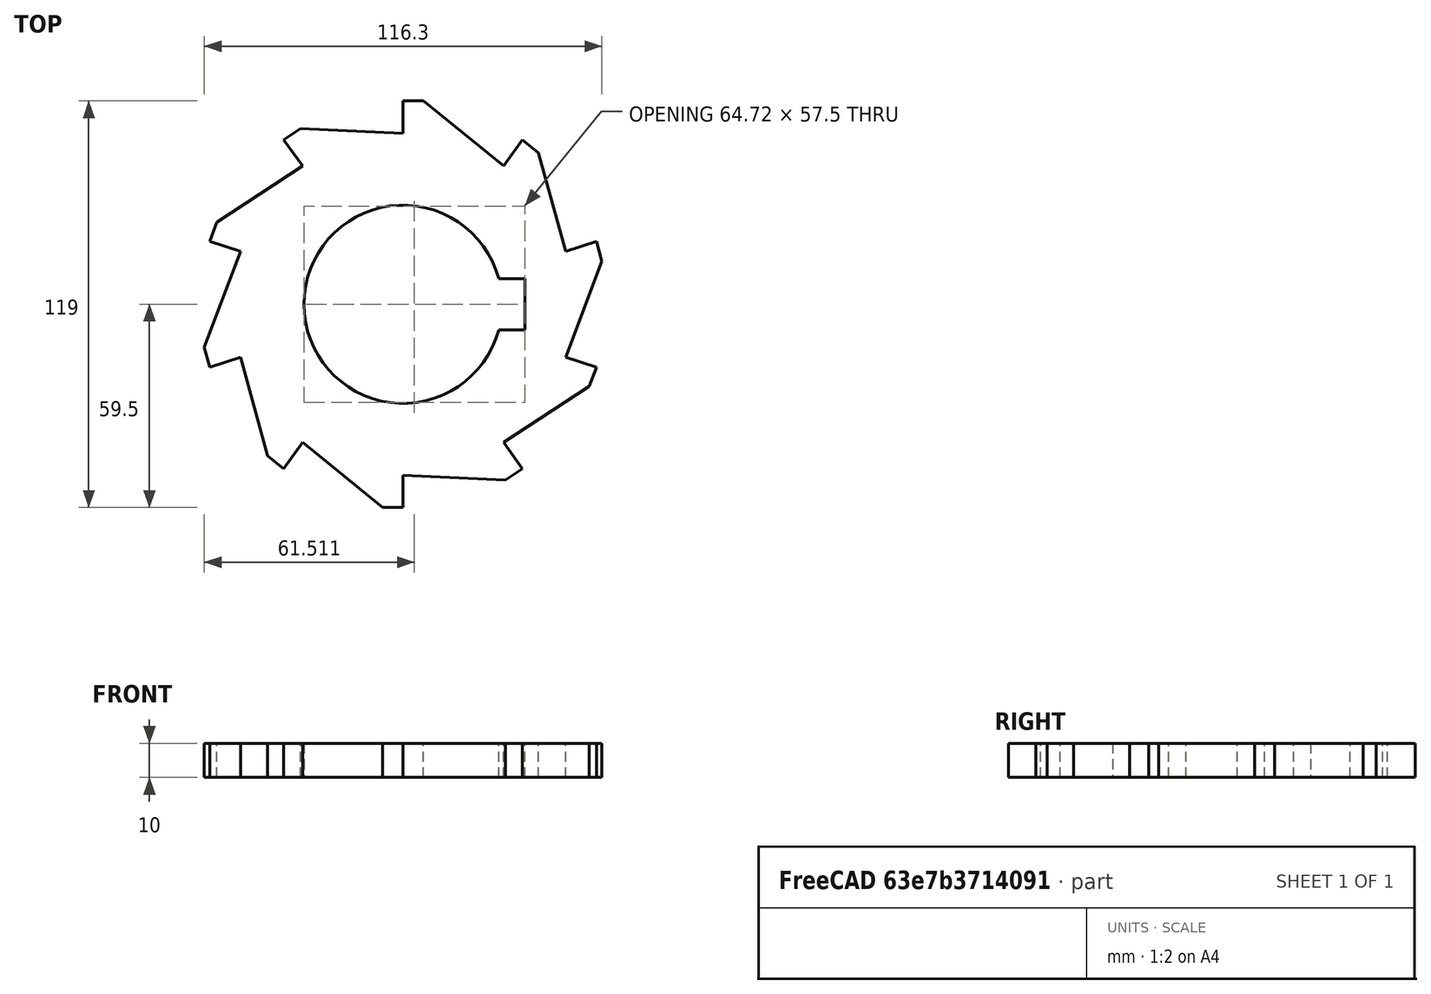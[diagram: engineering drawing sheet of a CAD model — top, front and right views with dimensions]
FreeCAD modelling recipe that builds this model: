
FCSTD DOCUMENT  (FreeCAD 0.20R29177 +426 (Git))
Label: 01 - Entrega de diseño de piezas
License: All rights reserved
LicenseURL: http://en.wikipedia.org/wiki/All_rights_reserved
objects: Sketcher::SketchObject×1, PartDesign::Pad×1, PartDesign::Body×1
note: 4 computed .brp shape members not serialized (recipe doc carries the construction recipe); baked Part::Feature solids carry a one-line shape summary decoded from their .brp

FEATURE [Sketcher::SketchObject] Sketch
  FullyConstrained = false
  MapMode = 5
  Support = -> [XY_Plane]
  sketch-geometry (47):
    g0: Circle CenterX=0 CenterY=0 CenterZ=0 NormalX=0 NormalY=0 NormalZ=1 AngleXU=0 Radius=59.5
    g1: ArcOfCircle CenterX=0 CenterY=0 CenterZ=0 NormalX=0 NormalY=0 NormalZ=1 AngleXU=0 Radius=29 StartAngle=0.261594 EndAngle=6.02159
    g2: LineSegment StartX=28.0134 StartY=7.5 StartZ=0 EndX=35.7211 EndY=7.5 EndZ=0
    g3: LineSegment StartX=35.7211 StartY=7.5 StartZ=0 EndX=35.7211 EndY=-7.5 EndZ=0
    g4: LineSegment StartX=35.7211 StartY=-7.5 StartZ=0 EndX=28.0134 EndY=-7.5 EndZ=0
    g5: Circle CenterX=0 CenterY=0 CenterZ=0 NormalX=0 NormalY=0 NormalZ=1 AngleXU=0 Radius=50
    g6: LineSegment StartX=-1.00329e-05 StartY=59.5 StartZ=0 EndX=5.99999 EndY=59.5 EndZ=0
    g7: LineSegment StartX=0 StartY=0 StartZ=0 EndX=81.4793 EndY=26.4742 EndZ=0
    g8: LineSegment StartX=0 StartY=0 StartZ=0 EndX=48.9757 EndY=67.4093 EndZ=0
    g9: LineSegment StartX=47.5528 StartY=15.4508 StartZ=0 EndX=56.5879 EndY=18.3865 EndZ=0
    g10: LineSegment StartX=0 StartY=0 StartZ=0 EndX=98.3194 EndY=0 EndZ=0
    g11: LineSegment StartX=0 StartY=0 StartZ=0 EndX=-40.9797 EndY=56.4037 EndZ=0
    g12: LineSegment StartX=0 StartY=0 StartZ=0 EndX=-69.3926 EndY=22.547 EndZ=0
    g13: LineSegment StartX=0 StartY=0 StartZ=0 EndX=-74.8837 EndY=-24.3312 EndZ=0
    g14: LineSegment StartX=0 StartY=0 StartZ=0 EndX=-41.6429 EndY=-57.3166 EndZ=0
    g15: LineSegment StartX=0 StartY=0 StartZ=0 EndX=-2.51e-14 EndY=-71.5915 EndZ=0
    g16: LineSegment StartX=0 StartY=0 StartZ=0 EndX=39.8031 EndY=-54.7843 EndZ=0
    g17: LineSegment StartX=0 StartY=0 StartZ=0 EndX=82.7007 EndY=-26.8711 EndZ=0
    g18: LineSegment StartX=56.5879 StartY=18.3865 StartZ=0 EndX=58.1519 EndY=12.5939 EndZ=0
    g19: LineSegment StartX=58.1519 StartY=12.5939 StartZ=0 EndX=47.5528 EndY=-15.4508 EndZ=0
    g20: LineSegment StartX=47.5528 StartY=-15.4508 StartZ=0 EndX=56.5879 EndY=-18.3865 EndZ=0
    g21: LineSegment StartX=56.5879 StartY=-18.3865 StartZ=0 EndX=54.4484 EndY=-23.9921 EndZ=0
    g22: LineSegment StartX=54.4484 StartY=-23.9921 StartZ=0 EndX=29.3893 EndY=-40.4508 EndZ=0
    g23: LineSegment StartX=29.3893 StartY=-40.4508 StartZ=0 EndX=34.9732 EndY=-48.1365 EndZ=0
    g24: LineSegment StartX=34.9732 StartY=-48.1365 StartZ=0 EndX=29.9475 EndY=-51.414 EndZ=0
    g25: LineSegment StartX=29.9475 StartY=-51.414 StartZ=0 EndX=-1.78e-14 EndY=-50 EndZ=0
    g26: LineSegment StartX=-1.78e-14 StartY=-50 StartZ=0 EndX=-2.09e-14 EndY=-59.5 EndZ=0
    g27: LineSegment StartX=-6 StartY=-59.5 StartZ=0 EndX=-29.3893 EndY=-40.4508 EndZ=0
    g28: LineSegment StartX=-47.5528 StartY=-15.4508 StartZ=0 EndX=-56.5879 EndY=-18.3865 EndZ=0
    g29: LineSegment StartX=-56.5879 StartY=-18.3865 StartZ=0 EndX=-58.1519 EndY=-12.5939 EndZ=0
    g30: LineSegment StartX=-58.1519 StartY=-12.5939 StartZ=0 EndX=-47.5528 EndY=15.4508 EndZ=0
    g31: LineSegment StartX=-47.5528 StartY=15.4508 StartZ=0 EndX=-56.5879 EndY=18.3865 EndZ=0
    g32: LineSegment StartX=-56.5879 StartY=18.3865 StartZ=0 EndX=-54.4484 EndY=23.9921 EndZ=0
    g33: LineSegment StartX=-54.4484 StartY=23.9921 StartZ=0 EndX=-29.3893 EndY=40.4508 EndZ=0
    g34: LineSegment StartX=-29.3893 StartY=40.4508 StartZ=0 EndX=-34.9732 EndY=48.1365 EndZ=0
    g35: LineSegment StartX=-2.09e-14 StartY=-59.5 StartZ=0 EndX=-6 EndY=-59.5 EndZ=0
    g36: LineSegment StartX=-34.9732 StartY=-48.1365 StartZ=0 EndX=-39.6433 EndY=-44.3695 EndZ=0
    g37: LineSegment StartX=-39.6433 StartY=-44.3695 StartZ=0 EndX=-47.5528 EndY=-15.4508 EndZ=0
    g38: LineSegment StartX=-34.9732 StartY=48.1365 StartZ=0 EndX=-29.9475 EndY=51.414 EndZ=0
    g39: LineSegment StartX=-29.9475 StartY=51.414 StartZ=0 EndX=-1.00329e-05 EndY=50 EndZ=0
    g40: Circle CenterX=0 CenterY=0 CenterZ=0 NormalX=0 NormalY=0 NormalZ=1 AngleXU=0 Radius=36.5
    g41: LineSegment StartX=-29.3893 StartY=-40.4508 StartZ=0 EndX=-34.9732 EndY=-48.1365 EndZ=0
    g42: LineSegment StartX=5.99999 StartY=59.5 StartZ=0 EndX=29.3893 EndY=40.4508 EndZ=0
    g43: LineSegment StartX=-1.00329e-05 StartY=59.5 StartZ=0 EndX=-1.00329e-05 EndY=50 EndZ=0
    g44: LineSegment StartX=34.9732 StartY=48.1365 StartZ=0 EndX=39.6433 EndY=44.3695 EndZ=0
    g45: LineSegment StartX=47.5528 StartY=15.4508 StartZ=0 EndX=39.6433 EndY=44.3695 EndZ=0
    g46: LineSegment StartX=34.9732 StartY=48.1365 StartZ=0 EndX=29.3893 EndY=40.4508 EndZ=0
  constraints (123):
    c: Diameter(g0) = 119
    c: Horizontal(g2)
    c: Coincident(g2,g3)
    c: Coincident(g3,g4)
    c: Horizontal(g4)
    c: Coincident(g1,g-1)
    c: DistanceY(g3,g3) = 15
    c: Symmetric(g2,g3,g-1)
    c: Coincident(g5,g1)
    c: PointOnObject(g6,g0)
    c: Horizontal(g6)
    c: Coincident(g7,g1)
    c: Angle(g-1,g7) = 0.314159
    c: Coincident(g8,g1)
    c: Angle(g-1,g8) = 0.942478
    c: PointOnObject(g44,g8)
    c: PointOnObject(g44,g0)
    c: Coincident(g0,g1)
    c: Distance(g6,g6) = 6
    c: PointOnObject(g9,g7)
    c: PointOnObject(g9,g5)
    c: PointOnObject(g9,g7)
    c: PointOnObject(g9,g0)
    c: Coincident(g1,g4)
    c: Coincident(g1,g2)
    c: Coincident(g10,g1)
    c: PointOnObject(g10,g-1)
    c: Coincident(g1,g11)
    c: Angle(g-2,g11) = 0.628319
    c: Coincident(g12,g1)
    c: Angle(g11,g12) = 0.628319
    c: Coincident(g13,g1)
    c: Angle(g12,g13) = 0.628319
    c: Coincident(g14,g1)
    c: Angle(g13,g14) = 0.628319
    c: Coincident(g15,g1)
    c: Angle(g14,g15) = 0.628319
    c: Coincident(g16,g1)
    c: Angle(g15,g16) = 0.628319
    c: Coincident(g17,g1)
    c: Angle(g16,g17) = 0.628319
    c: Coincident(g9,g18)
    c: Distance(g18) = 6
    c: PointOnObject(g18,g0)
    c: Coincident(g18,g19)
    c: PointOnObject(g19,g17)
    c: PointOnObject(g19,g5)
    c: Diameter(g5) = 100
    c: Coincident(g19,g20)
    c: PointOnObject(g20,g0)
    c: PointOnObject(g20,g17)
    c: Coincident(g20,g21)
    c: Distance(g21) = 6
    c: PointOnObject(g21,g0)
    c: Coincident(g21,g22)
    c: PointOnObject(g22,g16)
    c: PointOnObject(g22,g5)
    c: Coincident(g22,g23)
    c: PointOnObject(g23,g0)
    c: PointOnObject(g23,g16)
    c: Coincident(g23,g24)
    c: Distance(g24) = 6
    c: PointOnObject(g24,g0)
    c: Coincident(g24,g25)
    c: PointOnObject(g25,g15)
    c: PointOnObject(g25,g5)
    c: Coincident(g25,g26)
    c: PointOnObject(g26,g15)
    c: PointOnObject(g26,g0)
    c: PointOnObject(g27,g14)
    c: PointOnObject(g27,g5)
    c: PointOnObject(g28,g5)
    c: PointOnObject(g28,g13)
    c: PointOnObject(g28,g0)
    c: PointOnObject(g28,g13)
    c: Coincident(g28,g29)
    c: Distance(g29) = 6
    c: PointOnObject(g29,g0)
    c: Coincident(g29,g30)
    c: PointOnObject(g30,g12)
    c: PointOnObject(g30,g5)
    c: Coincident(g30,g31)
    c: PointOnObject(g31,g12)
    c: PointOnObject(g31,g0)
    c: Coincident(g31,g32)
    c: Distance(g32) = 6
    c: PointOnObject(g32,g0)
    c: Coincident(g32,g33)
    c: PointOnObject(g33,g11)
    c: PointOnObject(g33,g5)
    c: Coincident(g33,g34)
    c: PointOnObject(g34,g11)
    c: PointOnObject(g34,g0)
    c: Coincident(g35,g26)
    c: Horizontal(g35)
    c: DistanceX(g35,g35) = 6
    c: Coincident(g35,g27)
    c: Distance(g36) = 6
    c: PointOnObject(g36,g0)
    c: Coincident(g36,g37)
    c: Coincident(g37,g28)
    c: Coincident(g34,g38)
    c: Distance(g38) = 6
    c: PointOnObject(g38,g0)
    c: Coincident(g38,g39)
    c: Diameter(g1) = 58
    c: Coincident(g40,g1)
    c: Diameter(g40) = 73
    c: PointOnObject(g36,g14)
    c: PointOnObject(g36,g0)
    c: Coincident(g27,g41)
    c: Coincident(g41,g36)
    c: Coincident(g6,g42)
    c: Coincident(g43,g6)
    c: Coincident(g43,g39)
    c: Vertical(g43)
    c: Distance(g44) = 6
    c: PointOnObject(g44,g0)
    c: Coincident(g9,g45)
    c: Coincident(g45,g44)
    c: PointOnObject(g42,g8)
    c: PointOnObject(g42,g5)
    c: Coincident(g46,g42)
FEATURE [PartDesign::Pad] Pad
  Direction = (0,0,1)
  Length = 10
  Length2 = 10
  Profile = -> Sketch
  ReferenceAxis = -> Sketch [N_Axis]
  Type = 0
FEATURE [PartDesign::Body] Body
  Group = -> [Sketch,Pad]
  Origin = -> Origin
  Tip = -> Pad
